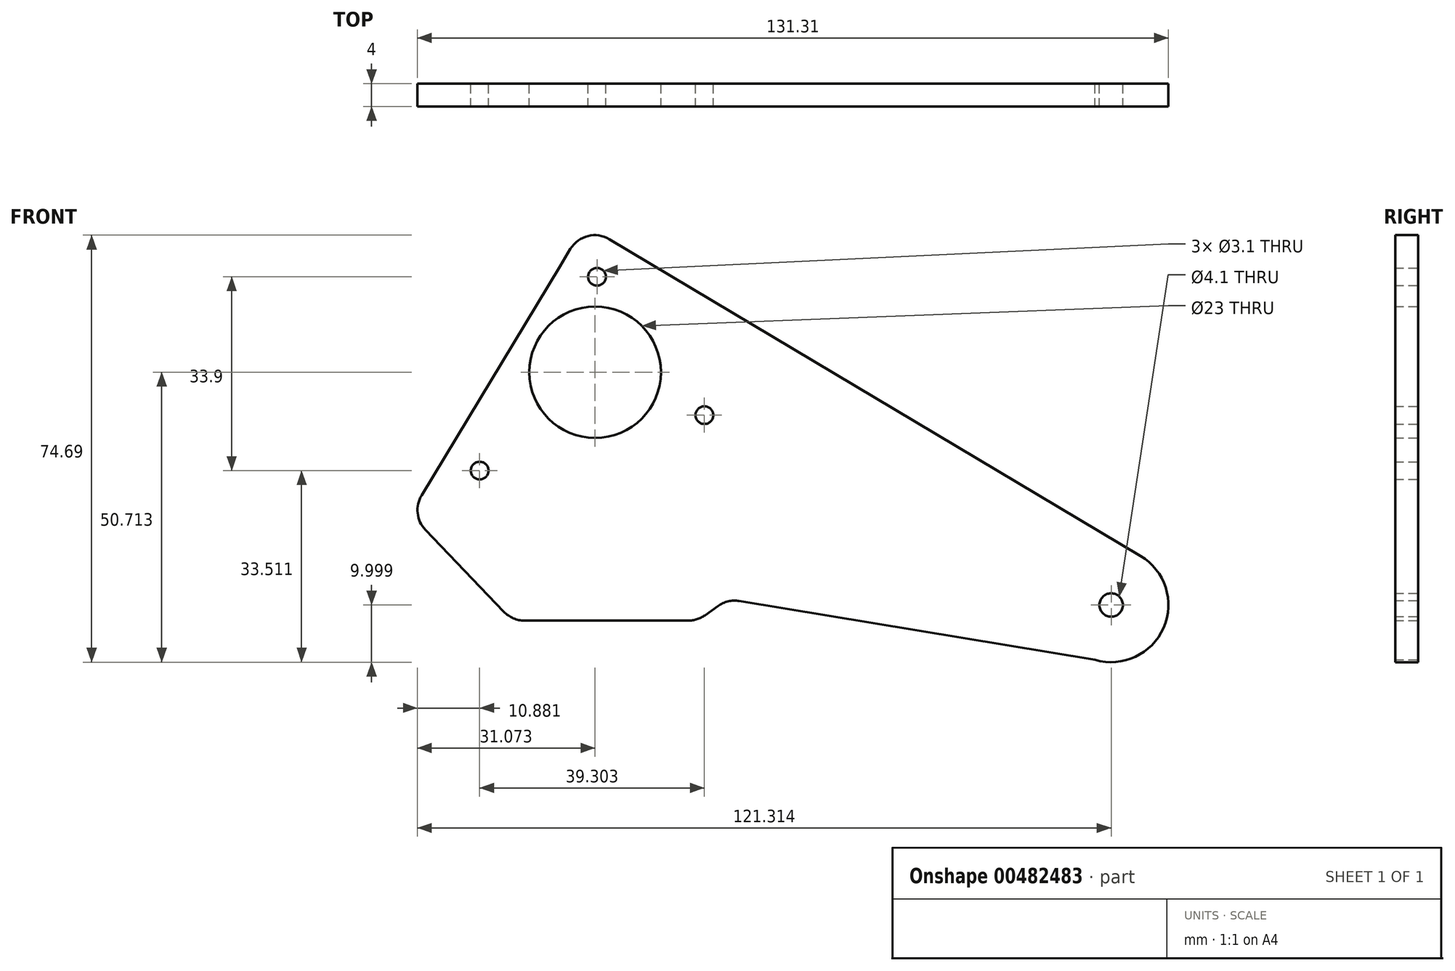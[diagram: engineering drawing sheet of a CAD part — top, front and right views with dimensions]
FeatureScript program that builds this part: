
annotation { "Feature Type Name" : "Feature", "Feature Type Description" : "" }
export const myFeature = defineFeature(function(context is Context, id is Id, definition is map)
    precondition{}
    {
        {
            var Q0;
            Q0=qCreatedBy(makeId("Front.planeOp"),FACE);
            var sketch = newSketch(context, id + "F0", { "sketchPlane" : qUnion([Q0])});
            skPoint(sketch, "E0", {"position": v(48.3, 10.49) * mm});
            skArc(sketch, "E1", {"start": v(45.48, 0.9) * mm, "mid": v(57.47, 6.48) * mm, "end": v(53.43, 19.08) * mm});
            skLineSegment(sketch, "E2", {"start": v(-16.38, 60.73) * mm, "end": v(53.43, 19.08) * mm});
            skPoint(sketch, "E3", {"position": v(-41.94, 51.2) * mm});
            skLineSegment(sketch, "E4", {"start": v(-72.29, 29.7) * mm, "end": v(-48.08, 69.76) * mm});
            skLineSegment(sketch, "E5", {"start": v(45.48, 0.9) * mm, "end": v(-16.73, 11.19) * mm});
            skLineSegment(sketch, "E6", {"start": v(-20.45, 10.32) * mm, "end": v(-22.73, 8.7) * mm});
            skLineSegment(sketch, "E7", {"start": v(-57.88, 9.3) * mm, "end": v(-71.62, 23.65) * mm});
            skLineSegment(sketch, "E8", {"start": v(-16.38, 60.73) * mm, "end": v(-39.42, 74.48) * mm});
            skLineSegment(sketch, "E9", {"start": v(-46.25, 72.77) * mm, "end": v(-48.08, 69.76) * mm});
            skPoint(sketch, "E10", {"position": v(-41.6, 67.9) * mm});
            skCircle(sketch, "E11", {"center": v(-41.94, 51.2) * mm, "radius": 11 * mm, "construction": true});
            skCircle(sketch, "E12", {"center": v(-41.6, 67.9) * mm, "radius": 4 * mm, "construction": true});
            skLineSegment(sketch, "E13", {"start": v(-54.27, 7.76) * mm, "end": v(-25.64, 7.76) * mm});
            skCircle(sketch, "E14", {"center": v(-22.83, 43.7) * mm, "radius": 4 * mm, "construction": true});
            skPoint(sketch, "E15", {"position": v(-61.83, 34) * mm});
            skCircle(sketch, "E16", {"center": v(-41.6, 67.9) * mm, "radius": 1.55 * mm});
            skCircle(sketch, "E17", {"center": v(-41.94, 51.2) * mm, "radius": 11.5 * mm});
            skCircle(sketch, "E18", {"center": v(-22.83, 43.7) * mm, "radius": 1.55 * mm});
            skCircle(sketch, "E19", {"center": v(48.3, 10.49) * mm, "radius": 2.05 * mm});
            skPoint(sketch, "E20.visualSharp", {"position": v(-74.27, 26.42) * mm});
            skArc(sketch, "E20.filletArc", {"start": v(-72.29, 29.7) * mm, "mid": v(-72.98, 26.56) * mm, "end": v(-71.62, 23.65) * mm});
            skPoint(sketch, "E21.visualSharp", {"position": v(-43.68, 77.02) * mm});
            skArc(sketch, "E21.filletArc", {"start": v(-39.42, 74.48) * mm, "mid": v(-43.19, 75.03) * mm, "end": v(-46.25, 72.77) * mm});
            skPoint(sketch, "E22.visualSharp", {"position": v(-56.4, 7.76) * mm});
            skArc(sketch, "E22.filletArc", {"start": v(-57.88, 9.3) * mm, "mid": v(-56.23, 8.16) * mm, "end": v(-54.27, 7.76) * mm});
            skPoint(sketch, "E23.visualSharp", {"position": v(-24.03, 7.76) * mm});
            skArc(sketch, "E23.filletArc", {"start": v(-25.64, 7.76) * mm, "mid": v(-24.1, 8) * mm, "end": v(-22.73, 8.7) * mm});
            skPoint(sketch, "E24.visualSharp", {"position": v(-18.77, 11.52) * mm});
            skArc(sketch, "E24.filletArc", {"start": v(-16.73, 11.19) * mm, "mid": v(-18.68, 11.12) * mm, "end": v(-20.45, 10.32) * mm});
            skPoint(sketch, "E25", {"position": v(-62.13, 34) * mm});
            skCircle(sketch, "E26", {"center": v(-62.13, 34) * mm, "radius": 1.55 * mm});
            skSolve(sketch);
        }
        {
            var Q0;
            Q0 = qSketchRegion(id + "F0", true);
            extrude(context, id + "F1", {"entities" : qUnion([Q0]), "depth" : 4 * mm, "offsetDistance" : 25 * mm});
        }
    });
